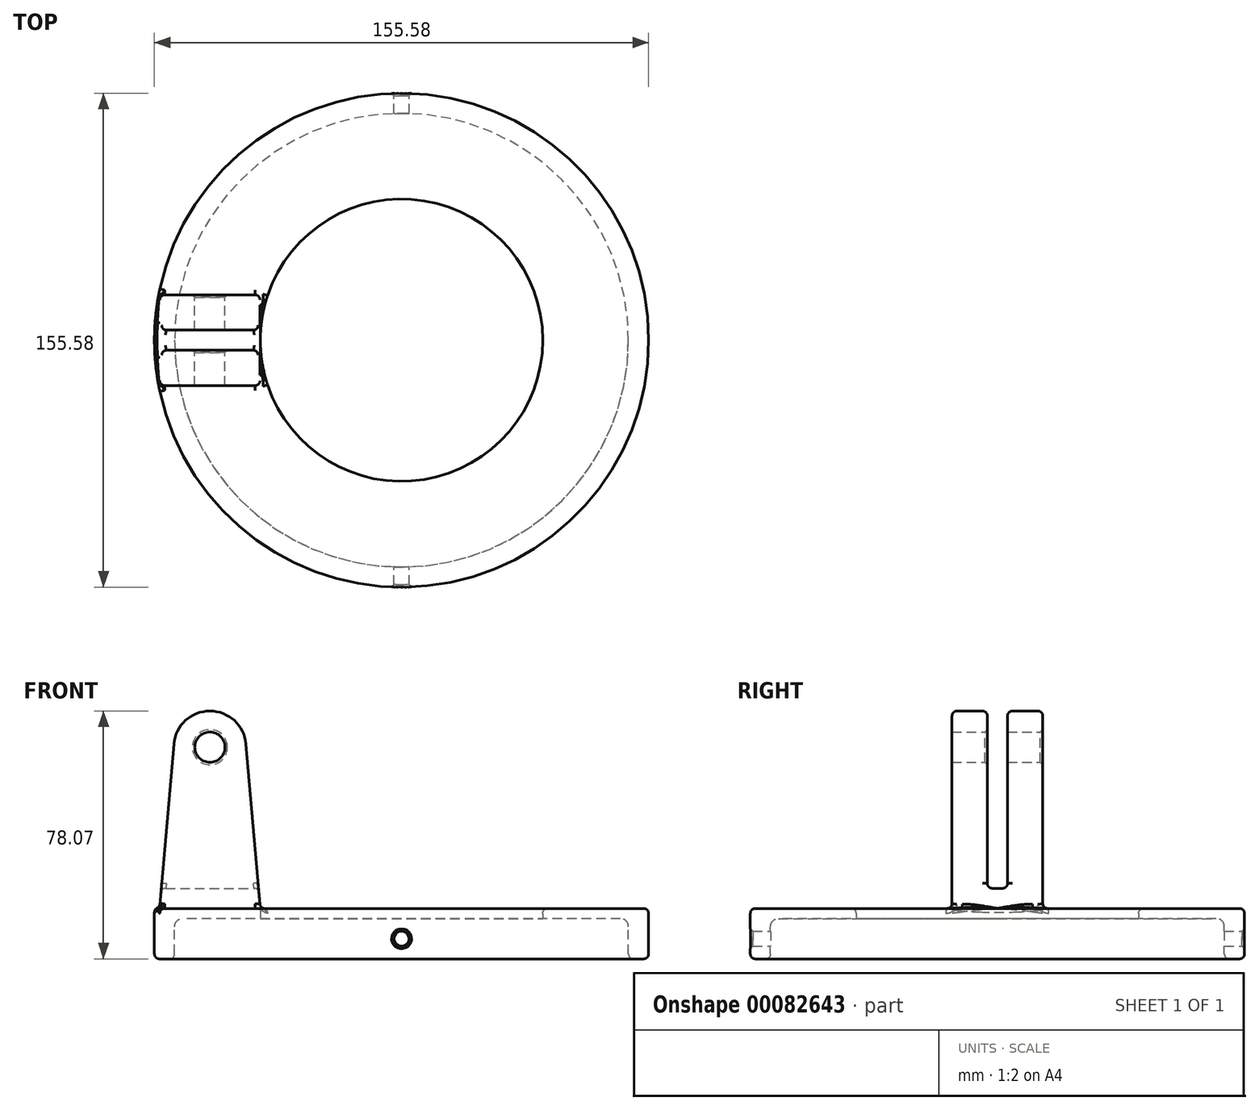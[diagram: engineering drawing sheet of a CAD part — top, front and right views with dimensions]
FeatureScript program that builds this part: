
annotation { "Feature Type Name" : "Feature", "Feature Type Description" : "" }
export const myFeature = defineFeature(function(context is Context, id is Id, definition is map)
    precondition{}
    {
        {
            var Q0;
            Q0=qCreatedBy(makeId("Front.planeOp"),FACE);
            var sketch = newSketch(context, id + "F0", { "sketchPlane" : qUnion([Q0])});
            skLineSegment(sketch, "E0", {"start": v(0, 0) * mm, "end": v(-77.79, 0) * mm});
            skLineSegment(sketch, "E1", {"start": v(-77.79, 0) * mm, "end": v(-77.79, -15.88) * mm});
            skLineSegment(sketch, "E2", {"start": v(-77.79, -15.88) * mm, "end": v(-71.44, -15.88) * mm});
            skLineSegment(sketch, "E3", {"start": v(-71.44, -15.88) * mm, "end": v(-71.44, -5.72) * mm});
            skLineSegment(sketch, "E4", {"start": v(-68.9, -3.18) * mm, "end": v(0, -3.18) * mm});
            skPoint(sketch, "E5.visualSharp", {"position": v(-71.44, -3.18) * mm});
            skArc(sketch, "E5.filletArc", {"start": v(-68.9, -3.18) * mm, "mid": v(-70.7, -3.92) * mm, "end": v(-71.44, -5.72) * mm});
            skLineSegment(sketch, "E6", {"start": v(0, 0) * mm, "end": v(0, -3.18) * mm});
            skLineSegment(sketch, "E7", {"start": v(0, -3.18) * mm, "end": v(0, -3.18) * mm});
            skSolve(sketch);
        }
        {
            var Q0;
            Q0=makeQuery(id+"F0.imprint","IMPRINT",FACE,{"disambiguationData":[TD([[makeQuery(id+"F0.imprint","IMPRINT",EDGE,{"derivedFrom":sQuery(id+"F0.wireOp",EDGE,"E0")}),1.0]])]});
            var Q1;
            Q1=sQuery(id+"F0.wireOp",EDGE,"E6");
            revolve(context, id + "F1", {"entities" : qUnion([Q0]), "axis" : qUnion([Q1]), "revolveType" : RevolveType.FULL});
        }
        {
            var Q0;
            Q0=makeQuery(id+"F1.opRevolve","SWEPT_FACE",FACE,{"disambiguationData":[OSD([sQuery(id+"F0.wireOp",EDGE,"E4")])]});
            var sketch = newSketch(context, id + "F2", { "sketchPlane" : qUnion([Q0])});
            skCircle(sketch, "E8", {"center": v(0, 0) * mm, "radius": 44.45 * mm});
            skLineSegment(sketch, "E9", {"start": v(-44.45, 0) * mm, "end": v(-44.45, -23.46) * mm});
            skLineSegment(sketch, "E10", {"start": v(-76.2, -14.3) * mm, "end": v(-76.2, -20.58) * mm});
            skSolve(sketch);
        }
        {
            var Q0;
            Q0 = qSketchRegion(id + "F2", true);
            extrude(context, id + "F3", {"entities" : qUnion([Q0]), "operationType" : NewBodyOperationType.REMOVE, "oppositeDirection" : true, "depth" : 76.2 * mm});
        }
        {
            var Q0;
            Q0=qCreatedBy(makeId("Front.planeOp"),FACE);
            var sketch = newSketch(context, id + "F4", { "sketchPlane" : qUnion([Q0])});
            skLineSegment(sketch, "E11", {"start": v(-76.2, 0) * mm, "end": v(-71.67, 51.8) * mm});
            skLineSegment(sketch, "E12", {"start": v(-48.98, 51.8) * mm, "end": v(-44.45, 0) * mm});
            skLineSegment(sketch, "E13", {"start": v(-76.2, 0) * mm, "end": v(-44.45, 0) * mm});
            skPoint(sketch, "E14", {"position": v(-60.33, 50.8) * mm});
            skArc(sketch, "E15", {"start": v(-71.67, 51.8) * mm, "mid": v(-60.33, 62.19) * mm, "end": v(-48.98, 51.8) * mm});
            skCircle(sketch, "E16", {"center": v(-60.33, 50.8) * mm, "radius": 4.76 * mm});
            skSolve(sketch);
        }
        {
            var Q0;
            Q0 = qSketchRegion(id + "F4", true);
            extrude(context, id + "F5", {"entities" : qUnion([Q0]), "operationType" : NewBodyOperationType.ADD, "endBound" : BoundingType.SYMMETRIC, "depth" : 28.57 * mm});
        }
        {
            var Q0;
            Q0=qCreatedBy(makeId("Right.planeOp"),FACE);
            var sketch = newSketch(context, id + "F6", { "sketchPlane" : qUnion([Q0])});
            skLineSegment(sketch, "E17.bottom", {"start": v(3.17, 77.5) * mm, "end": v(-3.18, 77.5) * mm});
            skLineSegment(sketch, "E17.top", {"start": v(3.18, 6.35) * mm, "end": v(-3.17, 6.35) * mm});
            skLineSegment(sketch, "E17.left", {"start": v(3.17, 77.5) * mm, "end": v(3.18, 6.35) * mm});
            skLineSegment(sketch, "E17.right", {"start": v(-3.18, 77.5) * mm, "end": v(-3.17, 6.35) * mm});
            skSolve(sketch);
        }
        {
            var Q0;
            Q0 = qSketchRegion(id + "F6", true);
            extrude(context, id + "F7", {"entities" : qUnion([Q0]), "operationType" : NewBodyOperationType.REMOVE, "oppositeDirection" : true, "depth" : 101.6 * mm});
        }
        {
            var Q0;
            Q0=makeQuery(id+"F7.boolean.opBoolean","COPY",EDGE,{"derivedFrom":makeQuery(id+"F7.opExtrude","SWEPT_EDGE",EDGE,{"disambiguationData":[OSD([sQuery(id+"F6.wireOp",EDGE,"E17.top"),sQuery(id+"F6.wireOp",EDGE,"E17.left")])]})});
            var Q1;
            Q1=makeQuery(id+"F7.boolean.opBoolean","COPY",EDGE,{"derivedFrom":makeQuery(id+"F7.opExtrude","SWEPT_EDGE",EDGE,{"disambiguationData":[OSD([sQuery(id+"F6.wireOp",EDGE,"E17.top"),sQuery(id+"F6.wireOp",EDGE,"E17.right")])]})});
            var Q2;
            Q2=makeQuery(id+"F5.opExtrude","CAP_EDGE",EDGE,{"disambiguationData":[OSD([sQuery(id+"F4.wireOp",EDGE,"E11")])],"isStart":true});
            var Q3;
            Q3=makeQuery(id+"F5.opExtrude","CAP_EDGE",EDGE,{"disambiguationData":[OSD([sQuery(id+"F4.wireOp",EDGE,"E15")])],"isStart":true});
            var Q4;
            Q4=makeQuery(id+"F5.opExtrude","CAP_EDGE",EDGE,{"disambiguationData":[OSD([sQuery(id+"F4.wireOp",EDGE,"E12")])],"isStart":true});
            var Q5;
            Q5=makeQuery(id+"F5.opExtrude","CAP_EDGE",EDGE,{"disambiguationData":[OSD([sQuery(id+"F4.wireOp",EDGE,"E15")])],"isStart":false});
            var Q6;
            Q6=makeQuery(id+"F5.opExtrude","CAP_EDGE",EDGE,{"disambiguationData":[OSD([sQuery(id+"F4.wireOp",EDGE,"E11")])],"isStart":false});
            var Q7;
            Q7=makeQuery(id+"F5.opExtrude","CAP_EDGE",EDGE,{"disambiguationData":[OSD([sQuery(id+"F4.wireOp",EDGE,"E12")])],"isStart":false});
            fillet(context, id + "F8", {"entities" : qUnion([Q0, Q1, Q2, Q3, Q4, Q5, Q6, Q7]), "radius" : 1.52 * mm, "tangentPropagation" : true, "allowEdgeOverflow" : false});
        }
        {
            var Q0;
            Q0=makeQuery(id+"F5.opExtrude","CAP_EDGE",EDGE,{"disambiguationData":[OSD([sQuery(id+"F4.wireOp",EDGE,"E13")])],"isStart":true});
            var Q1;
            Q1=makeQuery(id+"F5.opExtrude","SWEPT_FACE",FACE,{"disambiguationData":[OSD([sQuery(id+"F4.wireOp",EDGE,"E11")])]});
            fillet(context, id + "F9", {"entities" : qUnion([Q0, Q1]), "radius" : 1.52 * mm, "tangentPropagation" : true, "allowEdgeOverflow" : false});
        }
        {
            var Q0;
            Q0=makeQuery(id+"F3.boolean.opBoolean","INTERSECT",EDGE,{"derivedFrom":[makeQuery(id+"F1.opRevolve","SWEPT_FACE",FACE,{"disambiguationData":[OSD([sQuery(id+"F0.wireOp",EDGE,"E0")])]}),makeQuery(id+"F3.opExtrude","SWEPT_FACE",FACE,{"disambiguationData":[OSD([sQuery(id+"F2.wireOp",EDGE,"E8")])]})]});
            var Q1;
            Q1=makeQuery(id+"F3.boolean.opBoolean","COPY",EDGE,{"derivedFrom":makeQuery(id+"F3.opExtrude","CAP_EDGE",EDGE,{"disambiguationData":[OSD([sQuery(id+"F2.wireOp",EDGE,"E8")])],"isStart":true})});
            var Q2;
            Q2=makeQuery(id+"F1.opRevolve","SWEPT_EDGE",EDGE,{"disambiguationData":[OSD([sQuery(id+"F0.wireOp",EDGE,"E0"),sQuery(id+"F0.wireOp",EDGE,"E1")])]});
            var Q3;
            Q3=makeQuery(id+"F1.opRevolve","SWEPT_EDGE",EDGE,{"disambiguationData":[OSD([sQuery(id+"F0.wireOp",EDGE,"E1"),sQuery(id+"F0.wireOp",EDGE,"E2")])]});
            var Q4;
            Q4=makeQuery(id+"F1.opRevolve","SWEPT_EDGE",EDGE,{"disambiguationData":[OSD([sQuery(id+"F0.wireOp",EDGE,"E2"),sQuery(id+"F0.wireOp",EDGE,"E3")])]});
            fillet(context, id + "F10", {"entities" : qUnion([Q0, Q1, Q2, Q3, Q4]), "radius" : 1.52 * mm, "tangentPropagation" : true, "allowEdgeOverflow" : false});
        }
        {
            var Q0;
            Q0=qCreatedBy(makeId("Front.planeOp"),FACE);
            var sketch = newSketch(context, id + "F11", { "sketchPlane" : qUnion([Q0])});
            skPoint(sketch, "E18", {"position": v(0, -9.53) * mm});
            skCircle(sketch, "E19", {"center": v(0, -9.53) * mm, "radius": 2.38 * mm});
            skSolve(sketch);
        }
        {
            var Q0;
            Q0 = qSketchRegion(id + "F11", true);
            extrude(context, id + "F12", {"entities" : qUnion([Q0]), "operationType" : NewBodyOperationType.REMOVE, "endBound" : BoundingType.SYMMETRIC, "depth" : 165.1 * mm});
        }
        {
            var Q0;
            Q0=makeQuery(id+"F7.boolean.opBoolean","INTERSECT",EDGE,{"derivedFrom":[makeQuery(id+"F5.opExtrude","SWEPT_FACE",FACE,{"disambiguationData":[OSD([sQuery(id+"F4.wireOp",EDGE,"E16")])]}),makeQuery(id+"F7.opExtrude","SWEPT_FACE",FACE,{"disambiguationData":[OSD([sQuery(id+"F6.wireOp",EDGE,"E17.right")])]})]});
            var Q1;
            Q1=makeQuery(id+"F5.opExtrude","CAP_EDGE",EDGE,{"disambiguationData":[OSD([sQuery(id+"F4.wireOp",EDGE,"E16")])],"isStart":true});
            var Q2;
            Q2=makeQuery(id+"F12.boolean.opBoolean","INTERSECT",EDGE,{"disambiguationData":[OD(1.0)],"derivedFrom":[makeQuery(id+"F1.opRevolve","SWEPT_FACE",FACE,{"disambiguationData":[OSD([sQuery(id+"F0.wireOp",EDGE,"E1")])]}),makeQuery(id+"F12.opExtrude","SWEPT_FACE",FACE,{"disambiguationData":[OSD([sQuery(id+"F11.wireOp",EDGE,"E19")])]})]});
            var Q3;
            Q3=makeQuery(id+"F12.boolean.opBoolean","INTERSECT",EDGE,{"disambiguationData":[OD(0.0)],"derivedFrom":[makeQuery(id+"F1.opRevolve","SWEPT_FACE",FACE,{"disambiguationData":[OSD([sQuery(id+"F0.wireOp",EDGE,"E1")])]}),makeQuery(id+"F12.opExtrude","SWEPT_FACE",FACE,{"disambiguationData":[OSD([sQuery(id+"F11.wireOp",EDGE,"E19")])]})]});
            chamfer(context, id + "F13", {"entities" : qUnion([Q0, Q1, Q2, Q3]), "width" : 0.76 * mm, "tangentPropagation" : true});
        }
    });
